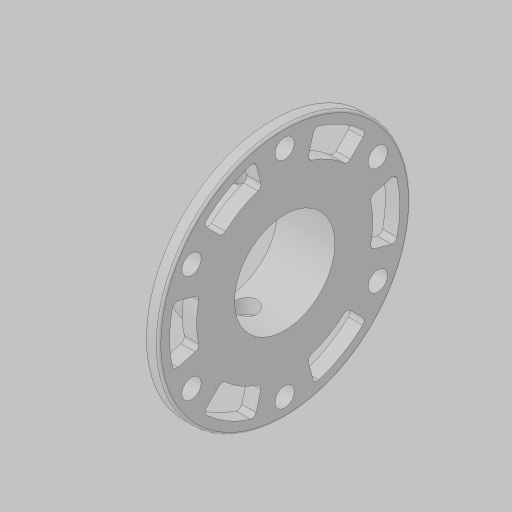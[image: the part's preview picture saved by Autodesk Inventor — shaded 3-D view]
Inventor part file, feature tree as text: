
AUTODESK INVENTOR PART (.ipt)
format: ipt  version: 2023.5 (Build 275446000, 446)  size: 232,448 bytes
history: native  units: in
note: dims shown in document units (in); Inventor stores cm internally (conversion verified against a paired STEP export)
features: sketch x2, hole x2, extrude x1, other x1
ambient origin geometry x8: Origin, YZ Plane, XZ Plane, XY Plane, X Axis, Y Axis, Z Axis, Center Point
bodies: Solid1 (feature_tree)
feature tree (6):
  extrude  "Extrusion1"  Depth=1.0in TaperAngle=0.0deg
  sketch  "Sketch2"  dims[d3=0.1562in d4=0.201in d5=0.38in d6=0.385in d7=0.25in d8=0.563in d9=1.0in d10=0.8108in d11=0.201in d12=0.75in d13=0.375in d14=0.25in d15=0.5635in d16=1.0in d17=0.8108in]
  hole  "Hole1"  [1 undecoded]
  hole  "Hole2"  [1 undecoded]
  sketch  "Sketch1"  dims[d0=0.875in d1=1.0in d2=0.0in]
  other  "Cut-Extrude8"
note: 2 required parameter values undecoded (feature->parameter linkage not recoverable at this tier; creation-order binding heuristic only, values carry confidence <= 0.55)
